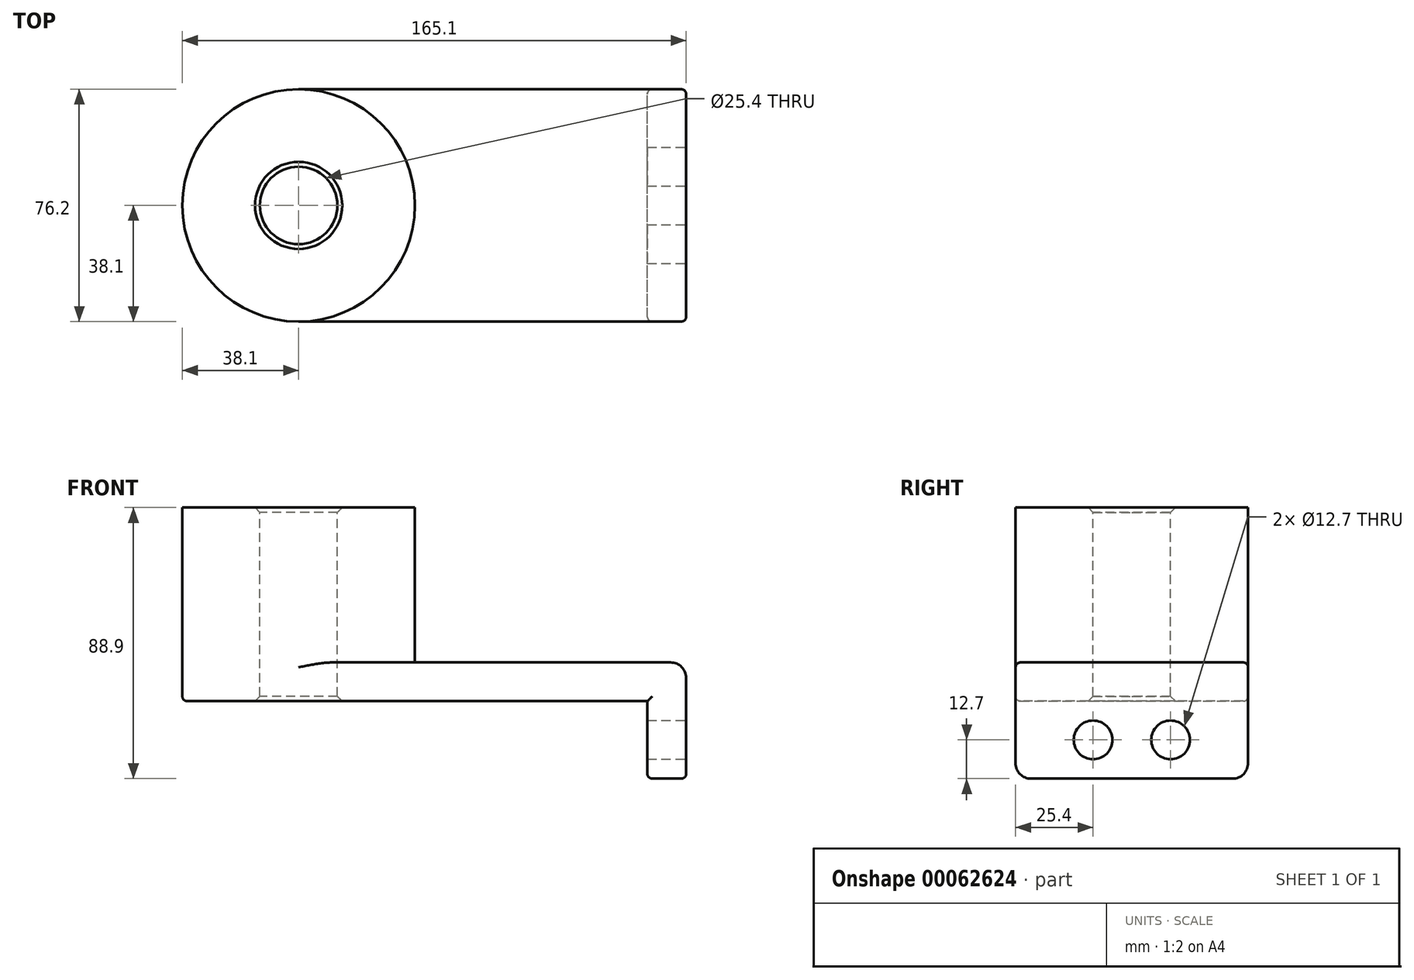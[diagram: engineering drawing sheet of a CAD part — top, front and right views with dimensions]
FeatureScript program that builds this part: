
annotation { "Feature Type Name" : "Feature", "Feature Type Description" : "" }
export const myFeature = defineFeature(function(context is Context, id is Id, definition is map)
    precondition{}
    {
        {
            var Q0;
            Q0=qCreatedBy(makeId("Top.planeOp"),FACE);
            var sketch = newSketch(context, id + "F0", { "sketchPlane" : qUnion([Q0])});
            skLineSegment(sketch, "E0.rect.bottom", {"start": v(63.5, 38.1) * mm, "end": v(-63.5, 38.1) * mm});
            skLineSegment(sketch, "E0.rect.top", {"start": v(63.5, -38.1) * mm, "end": v(-63.5, -38.1) * mm});
            skLineSegment(sketch, "E0.rect.left", {"start": v(63.5, 38.1) * mm, "end": v(63.5, -38.1) * mm});
            skLineSegment(sketch, "E0.rect.right", {"start": v(-63.5, 38.1) * mm, "end": v(-63.5, -38.1) * mm});
            skPoint(sketch, "E0.rect.middle", {"position": v(0, 0) * mm});
            skCircle(sketch, "E1", {"center": v(-63.5, 0) * mm, "radius": 38.1 * mm});
            skCircle(sketch, "E2", {"center": v(-63.5, 0) * mm, "radius": 12.7 * mm});
            skSolve(sketch);
        }
        {
            var Q0;
            Q0 = qSketchRegion(id + "F0", true);
            extrude(context, id + "F1", {"entities" : qUnion([Q0]), "oppositeDirection" : true, "depth" : 12.7 * mm});
        }
        {
            var Q0;
            {var subQ1=sQuery(id+"F0.wireOp",EDGE,"E0.rect.right");var subQ3=sQuery(id+"F0.wireOp",EDGE,"E2");var subQ4=makeQuery(id+"F0.imprint","INTERSECT",VERTEX,{"disambiguationData":[OD(0.0)],"derivedFrom":[subQ1,subQ3]});Q0=makeQuery(id+"F0.imprint","IMPRINT",FACE,{"disambiguationData":[TD([[makeQuery(id+"F0.imprint","IMPRINT",EDGE,{"disambiguationData":[TD([[subQ4,-1.0]])],"derivedFrom":subQ3}),-1.0]])]});}
            var Q1;
            {var subQ1=sQuery(id+"F0.wireOp",EDGE,"E0.rect.right");var subQ3=sQuery(id+"F0.wireOp",EDGE,"E2");var subQ4=makeQuery(id+"F0.imprint","INTERSECT",VERTEX,{"disambiguationData":[OD(0.0)],"derivedFrom":[subQ1,subQ3]});Q1=makeQuery(id+"F0.imprint","IMPRINT",FACE,{"disambiguationData":[TD([[makeQuery(id+"F0.imprint","IMPRINT",EDGE,{"disambiguationData":[TD([[subQ4,1.0]])],"derivedFrom":subQ3}),-1.0]])]});}
            extrude(context, id + "F2", {"entities" : qUnion([Q0, Q1]), "operationType" : NewBodyOperationType.ADD, "depth" : 50.8 * mm});
        }
        {
            var Q0;
            Q0=makeQuery(id+"F1.opExtrude","SWEPT_FACE",FACE,{"disambiguationData":[OSD([sQuery(id+"F0.wireOp",EDGE,"E0.rect.left")])]});
            var sketch = newSketch(context, id + "F3", { "sketchPlane" : qUnion([Q0])});
            skLineSegment(sketch, "E3.bottom", {"start": v(-38.1, 0) * mm, "end": v(38.1, 0) * mm});
            skLineSegment(sketch, "E3.top", {"start": v(-38.1, -38.1) * mm, "end": v(38.1, -38.1) * mm});
            skLineSegment(sketch, "E3.left", {"start": v(-38.1, 0) * mm, "end": v(-38.1, -38.1) * mm});
            skLineSegment(sketch, "E3.right", {"start": v(38.1, 0) * mm, "end": v(38.1, -38.1) * mm});
            skCircle(sketch, "E4", {"center": v(-12.7, -25.4) * mm, "radius": 6.35 * mm});
            skLineSegment(sketch, "E5", {"start": v(0, -12.7) * mm, "end": v(0, -38.1) * mm, "construction": true});
            skCircle(sketch, "E6.MirrorC", {"center": v(12.7, -25.4) * mm, "radius": 6.35 * mm});
            skSolve(sketch);
        }
        {
            var Q0;
            Q0 = qSketchRegion(id + "F3", true);
            extrude(context, id + "F4", {"entities" : qUnion([Q0]), "operationType" : NewBodyOperationType.ADD, "oppositeDirection" : true, "depth" : 12.7 * mm});
        }
        {
            var Q0;
            Q0=makeQuery(id+"F2.opExtrude","CAP_EDGE",EDGE,{"disambiguationData":[OSD([sQuery(id+"F0.wireOp",EDGE,"E1")])],"isStart":true});
            var Q1;
            Q1=makeQuery(id+"F4.opExtrude","SWEPT_EDGE",EDGE,{"disambiguationData":[OSD([sQuery(id+"F3.wireOp",EDGE,"E3.top"),sQuery(id+"F3.wireOp",EDGE,"E3.left")])]});
            var Q2;
            Q2=makeQuery(id+"F4.opExtrude","SWEPT_EDGE",EDGE,{"disambiguationData":[OSD([sQuery(id+"F3.wireOp",EDGE,"E3.top"),sQuery(id+"F3.wireOp",EDGE,"E3.right")])]});
            var Q3;
            Q3=makeQuery(id+"F1.opExtrude","CAP_EDGE",EDGE,{"disambiguationData":[OSD([sQuery(id+"F0.wireOp",EDGE,"E0.rect.left")])],"isStart":true});
            fillet(context, id + "F5", {"entities" : qUnion([Q0, Q1, Q2, Q3]), "radius" : 5.08 * mm, "tangentPropagation" : true, "allowEdgeOverflow" : false});
        }
        {
            var Q0;
            Q0=makeQuery(id+"F1.opExtrude","CAP_EDGE",EDGE,{"disambiguationData":[OSD([sQuery(id+"F0.wireOp",EDGE,"E0.rect.top")])],"isStart":true});
            var Q1;
            Q1=makeQuery(id+"F1.opExtrude","CAP_EDGE",EDGE,{"disambiguationData":[OSD([sQuery(id+"F0.wireOp",EDGE,"E0.rect.bottom")])],"isStart":false});
            fillet(context, id + "F6", {"entities" : qUnion([Q0, Q1]), "radius" : 1.59 * mm, "tangentPropagation" : true, "allowEdgeOverflow" : false});
        }
        {
            var Q0;
            Q0=makeQuery(id+"F4.opExtrude","CAP_EDGE",EDGE,{"disambiguationData":[OSD([sQuery(id+"F3.wireOp",EDGE,"E3.top")])],"isStart":false});
            fillet(context, id + "F7", {"entities" : qUnion([Q0]), "radius" : 1.59 * mm, "tangentPropagation" : true, "allowEdgeOverflow" : false});
        }
        {
            var Q0;
            {var subQ0=sQuery(id+"F0.wireOp",EDGE,"E2");Q0=makeQuery(id+"F2.boolean.opBoolean","MERGE",FACE,{"derivedFrom":[makeQuery(id+"F1.opExtrude","SWEPT_FACE",FACE,{"disambiguationData":[OSD([subQ0])]}),makeQuery(id+"F2.opExtrude","SWEPT_FACE",FACE,{"disambiguationData":[OSD([subQ0])]})]});}
            var Q1;
            {var subQ0=sQuery(id+"F0.wireOp",EDGE,"E0.rect.top");Q1=makeQuery(id+"F6.opFillet","BLEND_EDGE",EDGE,{"blendedFrom":[makeQuery(id+"F1.opExtrude","CAP_EDGE",EDGE,{"disambiguationData":[OSD([subQ0])],"isStart":false}),makeQuery(id+"F4.boolean.opBoolean","MERGE",FACE,{"derivedFrom":[makeQuery(id+"F1.opExtrude","SWEPT_FACE",FACE,{"disambiguationData":[OSD([subQ0])]}),makeQuery(id+"F4.opExtrude","SWEPT_FACE",FACE,{"disambiguationData":[OSD([sQuery(id+"F3.wireOp",EDGE,"E3.left")])]})]})],"blendedInto":[makeQuery(id+"F4.boolean.opBoolean","MERGE",FACE,{"derivedFrom":[makeQuery(id+"F1.opExtrude","SWEPT_FACE",FACE,{"disambiguationData":[OSD([subQ0])]}),makeQuery(id+"F4.opExtrude","SWEPT_FACE",FACE,{"disambiguationData":[OSD([sQuery(id+"F3.wireOp",EDGE,"E3.left")])]})]})]});}
            var Q2;
            {var subQ0=sQuery(id+"F0.wireOp",EDGE,"E0.rect.top");Q2=makeQuery(id+"F6.opFillet","BLEND_EDGE",EDGE,{"blendedFrom":[makeQuery(id+"F1.opExtrude","CAP_EDGE",EDGE,{"disambiguationData":[OSD([subQ0])],"isStart":false}),makeQuery(id+"F1.opExtrude","CAP_FACE",FACE,{"disambiguationData":[OSD([sQuery(id+"F0.wireOp",EDGE,"E0.rect.bottom"),subQ0,sQuery(id+"F0.wireOp",EDGE,"E0.rect.left"),sQuery(id+"F0.wireOp",EDGE,"E1"),sQuery(id+"F0.wireOp",EDGE,"E2")])],"isStart":false})],"blendedInto":[makeQuery(id+"F1.opExtrude","CAP_FACE",FACE,{"disambiguationData":[OSD([sQuery(id+"F0.wireOp",EDGE,"E0.rect.bottom"),subQ0,sQuery(id+"F0.wireOp",EDGE,"E0.rect.left"),sQuery(id+"F0.wireOp",EDGE,"E1"),sQuery(id+"F0.wireOp",EDGE,"E2")])],"isStart":false})]});}
            var Q3;
            {var subQ0=sQuery(id+"F0.wireOp",EDGE,"E0.rect.top");Q3=makeQuery(id+"F6.opFillet","BLEND_EDGE",EDGE,{"blendedFrom":[makeQuery(id+"F1.opExtrude","CAP_EDGE",EDGE,{"disambiguationData":[OSD([subQ0])],"isStart":true}),makeQuery(id+"F1.opExtrude","CAP_FACE",FACE,{"disambiguationData":[OSD([sQuery(id+"F0.wireOp",EDGE,"E0.rect.bottom"),subQ0,sQuery(id+"F0.wireOp",EDGE,"E0.rect.left"),sQuery(id+"F0.wireOp",EDGE,"E1"),sQuery(id+"F0.wireOp",EDGE,"E2")])],"isStart":true})],"blendedInto":[makeQuery(id+"F1.opExtrude","CAP_FACE",FACE,{"disambiguationData":[OSD([sQuery(id+"F0.wireOp",EDGE,"E0.rect.bottom"),subQ0,sQuery(id+"F0.wireOp",EDGE,"E0.rect.left"),sQuery(id+"F0.wireOp",EDGE,"E1"),sQuery(id+"F0.wireOp",EDGE,"E2")])],"isStart":true})]});}
            var Q4;
            {var subQ0=sQuery(id+"F0.wireOp",EDGE,"E0.rect.top");Q4=makeQuery(id+"F6.opFillet","BLEND_EDGE",EDGE,{"blendedFrom":[makeQuery(id+"F1.opExtrude","CAP_EDGE",EDGE,{"disambiguationData":[OSD([subQ0])],"isStart":true}),makeQuery(id+"F4.boolean.opBoolean","MERGE",FACE,{"derivedFrom":[makeQuery(id+"F1.opExtrude","SWEPT_FACE",FACE,{"disambiguationData":[OSD([subQ0])]}),makeQuery(id+"F4.opExtrude","SWEPT_FACE",FACE,{"disambiguationData":[OSD([sQuery(id+"F3.wireOp",EDGE,"E3.left")])]})]})],"blendedInto":[makeQuery(id+"F4.boolean.opBoolean","MERGE",FACE,{"derivedFrom":[makeQuery(id+"F1.opExtrude","SWEPT_FACE",FACE,{"disambiguationData":[OSD([subQ0])]}),makeQuery(id+"F4.opExtrude","SWEPT_FACE",FACE,{"disambiguationData":[OSD([sQuery(id+"F3.wireOp",EDGE,"E3.left")])]})]})]});}
            chamfer(context, id + "F8", {"entities" : qUnion([Q0, Q1, Q2, Q3, Q4]), "width" : 1.59 * mm, "tangentPropagation" : true});
        }
    });
